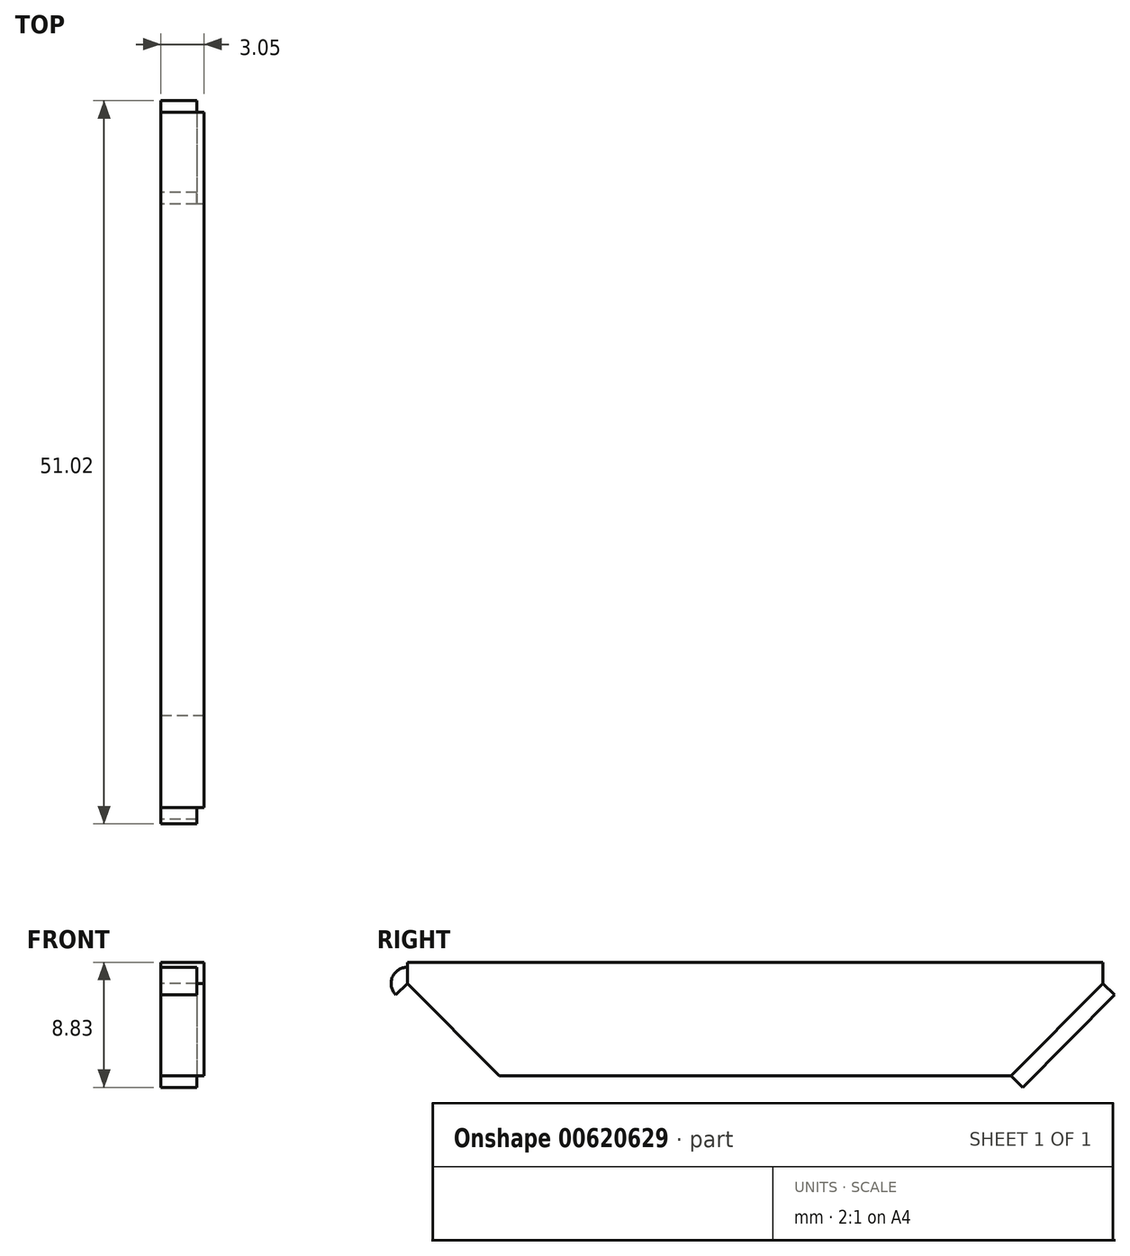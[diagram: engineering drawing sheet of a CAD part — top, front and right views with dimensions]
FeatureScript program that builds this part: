
annotation { "Feature Type Name" : "Feature", "Feature Type Description" : "" }
export const myFeature = defineFeature(function(context is Context, id is Id, definition is map)
    precondition{}
    {
        {
            var Q0;
            Q0=qCreatedBy(makeId("Right.planeOp"),FACE);
            var sketch = newSketch(context, id + "F0", { "sketchPlane" : qUnion([Q0])});
            skLineSegment(sketch, "E0", {"start": v(0, 0) * mm, "end": v(18.06, 0) * mm});
            skLineSegment(sketch, "E1", {"start": v(0, 0) * mm, "end": v(-18.06, 0) * mm});
            skLineSegment(sketch, "E2", {"start": v(0, 8.03) * mm, "end": v(-24.53, 8.03) * mm});
            skLineSegment(sketch, "E3", {"start": v(0, 8.03) * mm, "end": v(24.54, 8.03) * mm});
            skLineSegment(sketch, "E4", {"start": v(-24.53, 8.03) * mm, "end": v(-24.53, 6.53) * mm});
            skLineSegment(sketch, "E5", {"start": v(-24.53, 6.53) * mm, "end": v(-18.06, 0) * mm});
            skLineSegment(sketch, "E6", {"start": v(24.54, 8.03) * mm, "end": v(24.54, 6.53) * mm});
            skLineSegment(sketch, "E7", {"start": v(24.54, 6.53) * mm, "end": v(18.06, 0) * mm});
            skLineSegment(sketch, "E8", {"start": v(-18.06, 0) * mm, "end": v(18.06, 0) * mm});
            skLineSegment(sketch, "E9", {"start": v(-18.06, 0) * mm, "end": v(-18.87, -0.8) * mm});
            skLineSegment(sketch, "E10", {"start": v(-24.53, 6.53) * mm, "end": v(-25.35, 5.72) * mm});
            skLineSegment(sketch, "E11", {"start": v(-25.35, 5.72) * mm, "end": v(-18.87, -0.8) * mm});
            skLineSegment(sketch, "E12", {"start": v(18.06, 0) * mm, "end": v(18.87, -0.8) * mm});
            skLineSegment(sketch, "E13", {"start": v(24.54, 6.53) * mm, "end": v(25.34, 5.73) * mm});
            skLineSegment(sketch, "E14", {"start": v(25.34, 5.73) * mm, "end": v(18.87, -0.8) * mm});
            skArc(sketch, "E15", {"start": v(-24.53, 7.67) * mm, "mid": v(-25.59, 6.97) * mm, "end": v(-25.34, 5.72) * mm});
            skArc(sketch, "E16", {"start": v(24.54, 7.66) * mm, "mid": v(25.58, 6.96) * mm, "end": v(25.34, 5.73) * mm});
            skArc(sketch, "E17", {"start": v(-18.87, -0.8) * mm, "mid": v(-18.5, -1.05) * mm, "end": v(-18.06, -1.14) * mm});
            skArc(sketch, "E18", {"start": v(18.87, -0.8) * mm, "mid": v(18.5, -1.05) * mm, "end": v(18.06, -1.14) * mm});
            skLineSegment(sketch, "E19", {"start": v(-18.06, -1.14) * mm, "end": v(18.06, -1.14) * mm});
            skSolve(sketch);
        }
        {
            var Q0;
            Q0=makeQuery(id+"F0.imprint","IMPRINT",FACE,{"disambiguationData":[TD([[makeQuery(id+"F0.imprint","IMPRINT",EDGE,{"derivedFrom":sQuery(id+"F0.wireOp",EDGE,"E2")}),1.0]])]});
            extrude(context, id + "F1", {"entities" : qUnion([Q0]), "depth" : 3.05 * mm, "offsetDistance" : 25.4 * mm});
        }
        {
            var Q0;
            {var subQ3=sQuery(id+"F0.wireOp",EDGE,"E15");Q0=makeQuery(id+"F0.imprint","IMPRINT",FACE,{"disambiguationData":[TD([[makeQuery(id+"F0.imprint","IMPRINT",EDGE,{"derivedFrom":subQ3}),1.0]])]});}
            var Q1;
            {var subQ3=sQuery(id+"F0.wireOp",EDGE,"E5");Q1=makeQuery(id+"F0.imprint","IMPRINT",FACE,{"disambiguationData":[TD([[makeQuery(id+"F0.imprint","IMPRINT",EDGE,{"derivedFrom":subQ3}),-1.0]])]});}
            var Q2;
            Q2=makeQuery(id+"F0.imprint","IMPRINT",FACE,{"disambiguationData":[TD([[makeQuery(id+"F0.imprint","IMPRINT",EDGE,{"derivedFrom":sQuery(id+"F0.wireOp",EDGE,"E8")}),-1.0]])]});
            var Q3;
            {var subQ3=sQuery(id+"F0.wireOp",EDGE,"E7");Q3=makeQuery(id+"F0.imprint","IMPRINT",FACE,{"disambiguationData":[TD([[makeQuery(id+"F0.imprint","IMPRINT",EDGE,{"derivedFrom":subQ3}),1.0]])]});}
            var Q4;
            {var subQ3=sQuery(id+"F0.wireOp",EDGE,"E16");Q4=makeQuery(id+"F0.imprint","IMPRINT",FACE,{"disambiguationData":[TD([[makeQuery(id+"F0.imprint","IMPRINT",EDGE,{"derivedFrom":subQ3}),-1.0]])]});}
            extrude(context, id + "F2", {"entities" : qUnion([Q0, Q1, Q2, Q3, Q4]), "operationType" : NewBodyOperationType.ADD, "depth" : 2.54 * mm, "offsetDistance" : 25.4 * mm});
        }
    });
